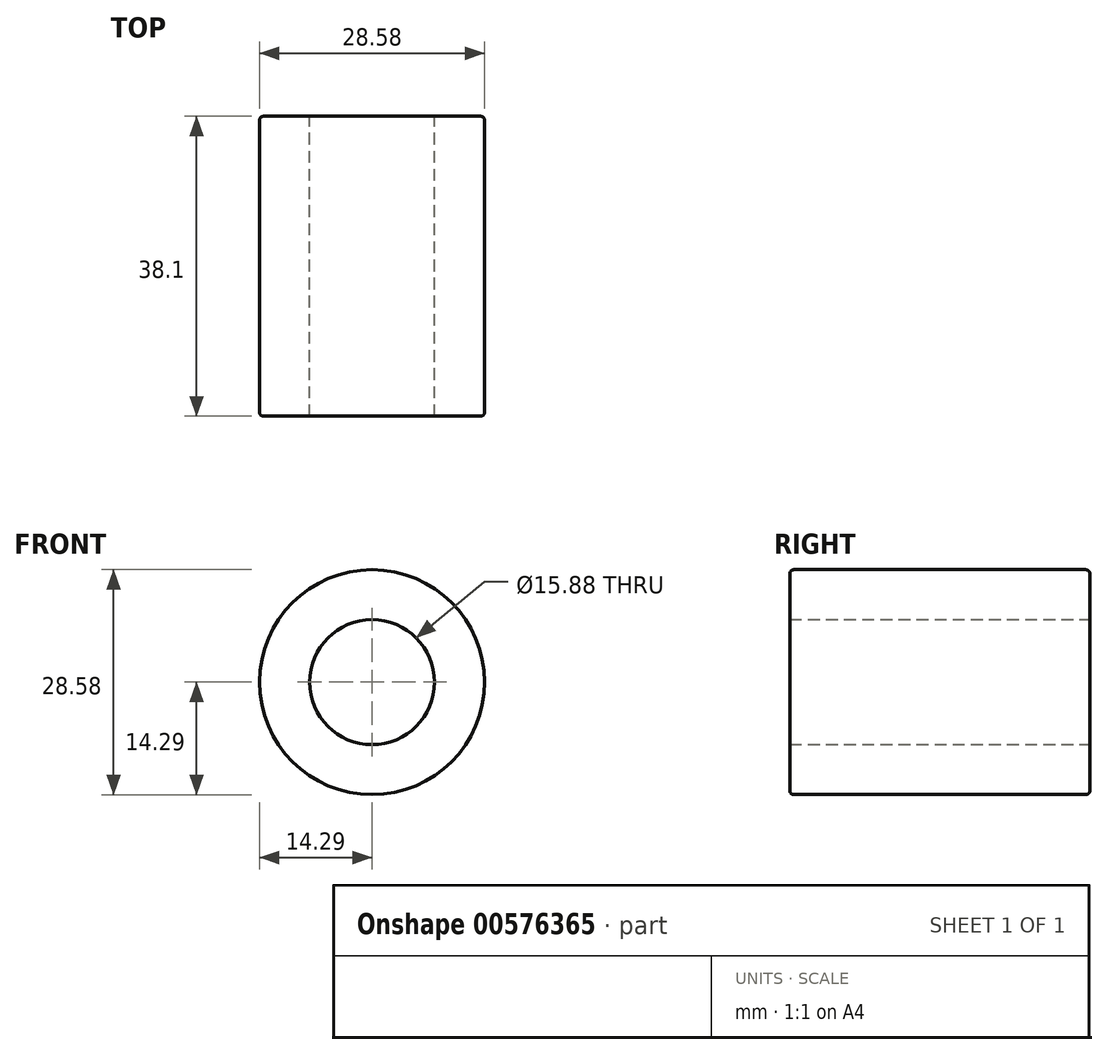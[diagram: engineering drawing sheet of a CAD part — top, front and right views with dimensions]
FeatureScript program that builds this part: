
annotation { "Feature Type Name" : "Feature", "Feature Type Description" : "" }
export const myFeature = defineFeature(function(context is Context, id is Id, definition is map)
    precondition{}
    {
        {
            var Q0;
            Q0=qCreatedBy(makeId("Front.planeOp"),FACE);
            var sketch = newSketch(context, id + "F0", { "sketchPlane" : qUnion([Q0]), "asVersion" : FeatureScriptVersionNumber.V686_LOFT_FS_BUG_FIXES});
            skCircle(sketch, "E0", {"center": v(0, 0) * mm, "radius": 7.94 * mm});
            skCircle(sketch, "E1", {"center": v(0, 0) * mm, "radius": 14.29 * mm});
            skSolve(sketch);
        }
        {
            var Q0;
            Q0 = qSketchRegion(id + "F0", true);
            extrude(context, id + "F1", {"entities" : qUnion([Q0]), "depth" : 38.1 * mm, "offsetDistance" : 25 * mm, "symmetric" : true});
        }
        {
            var Q0;
            Q0=makeQuery(id+"F1.opExtrude","CAP_EDGE",EDGE,{"disambiguationData":[OSD([sQuery(id+"F0.wireOp",EDGE,"E1")])],"isStart":false});
            var Q1;
            Q1=makeQuery(id+"F1.opExtrude","CAP_EDGE",EDGE,{"disambiguationData":[OSD([sQuery(id+"F0.wireOp",EDGE,"E1")])],"isStart":true});
            fillet(context, id + "F2", {"entities" : qUnion([Q0, Q1]), "radius" : 0.5 * mm, "tangentPropagation" : true, "allowEdgeOverflow" : false});
        }
    });
